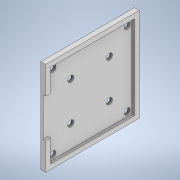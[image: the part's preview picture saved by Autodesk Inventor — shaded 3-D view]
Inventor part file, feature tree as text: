
AUTODESK INVENTOR PART (.ipt)
format: ipt  version: 2022 (Build 260153000, 153)  size: 142,848 bytes
history: native  units: mm
features: extrude x3, sketch x3
ambient origin geometry x8: Origin, YZ Plane, XZ Plane, XY Plane, X Axis, Y Axis, Z Axis, Center Point
bodies: Body1 (feature_tree)
feature tree (6):
  extrude  "Extrusion3"  Depth=30.75mm
  extrude  "Extrusion4"  Depth=2.0mm
  extrude  "Extrusion5"  Depth=1.0mm
  sketch  "Sketch1"  dims[d0=30.75mm d1=30.75mm]
  sketch  "Sketch3"  dims[d2=2.0mm d3=2.5mm]
  sketch  "Sketch4"  dims[d4=2.0mm d14=2.5mm d15=1.0mm d16=0.0mm d17=2.0mm d18=1.0mm d19=0.0mm d20=8.0mm d21=16.0mm d22=1.0mm d23=0.0mm]
